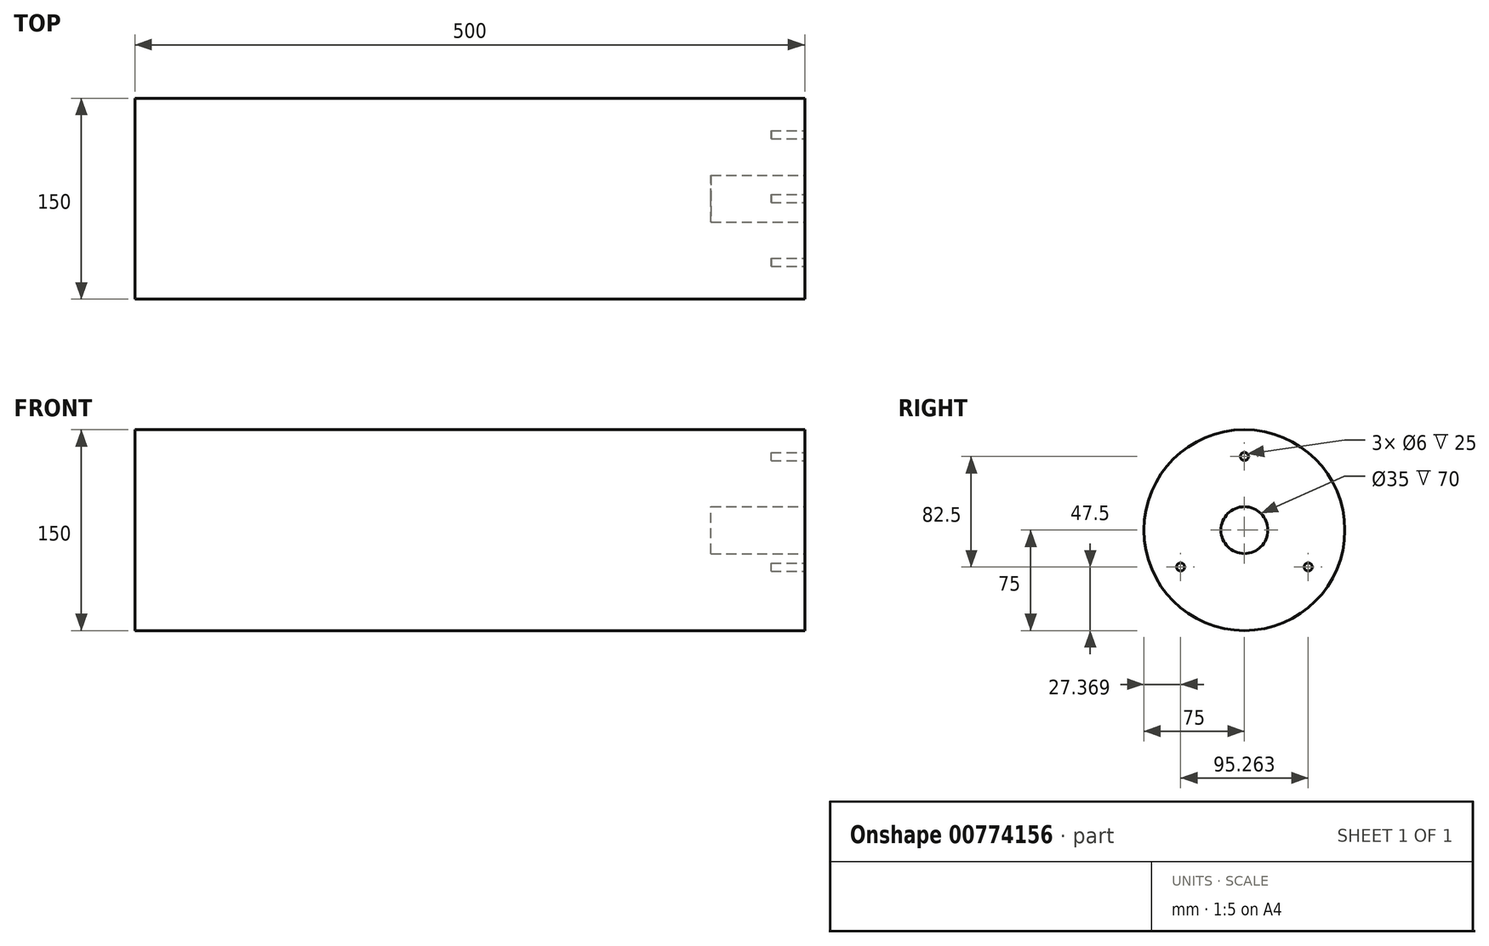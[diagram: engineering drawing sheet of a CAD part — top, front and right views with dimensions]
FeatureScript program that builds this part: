
annotation { "Feature Type Name" : "Feature", "Feature Type Description" : "" }
export const myFeature = defineFeature(function(context is Context, id is Id, definition is map)
    precondition{}
    {
        {
            var Q0;
            Q0=qCreatedBy(makeId("Front.planeOp"),FACE);
            var sketch = newSketch(context, id + "F0", { "sketchPlane" : qUnion([Q0])});
            skLineSegment(sketch, "E0", {"start": v(0, -75) * mm, "end": v(0, -17.5) * mm});
            skLineSegment(sketch, "E1", {"start": v(0, -17.5) * mm, "end": v(-70, -17.5) * mm});
            skLineSegment(sketch, "E2", {"start": v(-70, -17.5) * mm, "end": v(-70, 0) * mm});
            skLineSegment(sketch, "E3", {"start": v(-70, 0) * mm, "end": v(-500, 0) * mm});
            skLineSegment(sketch, "E4", {"start": v(-500, 0) * mm, "end": v(-500, -75) * mm});
            skLineSegment(sketch, "E5", {"start": v(-500, -75) * mm, "end": v(0, -75) * mm});
            skSolve(sketch);
        }
        {
            var Q0;
            Q0 = qSketchRegion(id + "F0", true);
            var Q1;
            Q1=sQuery(id+"F0.wireOp",EDGE,"E3");
            revolve(context, id + "F1", {"surfaceOperationType" : NewSurfaceOperationType.NEW, "entities" : qUnion([Q0]), "axis" : qUnion([Q1]), "revolveType" : RevolveType.FULL});
        }
        {
            var Q0;
            Q0=qCreatedBy(makeId("Right.planeOp"),FACE);
            var sketch = newSketch(context, id + "F2", { "sketchPlane" : qUnion([Q0])});
            skCircle(sketch, "E6", {"center": v(0, 55) * mm, "radius": 3 * mm});
            skCircle(sketch, "E7.1.0", {"center": v(-47.63, -27.5) * mm, "radius": 3 * mm});
            skCircle(sketch, "E7.2.0", {"center": v(47.63, -27.5) * mm, "radius": 3 * mm});
            skPoint(sketch, "E7.center", {"position": v(0, 0) * mm});
            skSolve(sketch);
        }
        {
            var Q0;
            Q0 = qSketchRegion(id + "F2", true);
            extrude(context, id + "F3", {"entities" : qUnion([Q0]), "operationType" : NewBodyOperationType.REMOVE, "oppositeDirection" : true, "depth" : 25 * mm, "offsetDistance" : 25 * mm});
        }
    });
